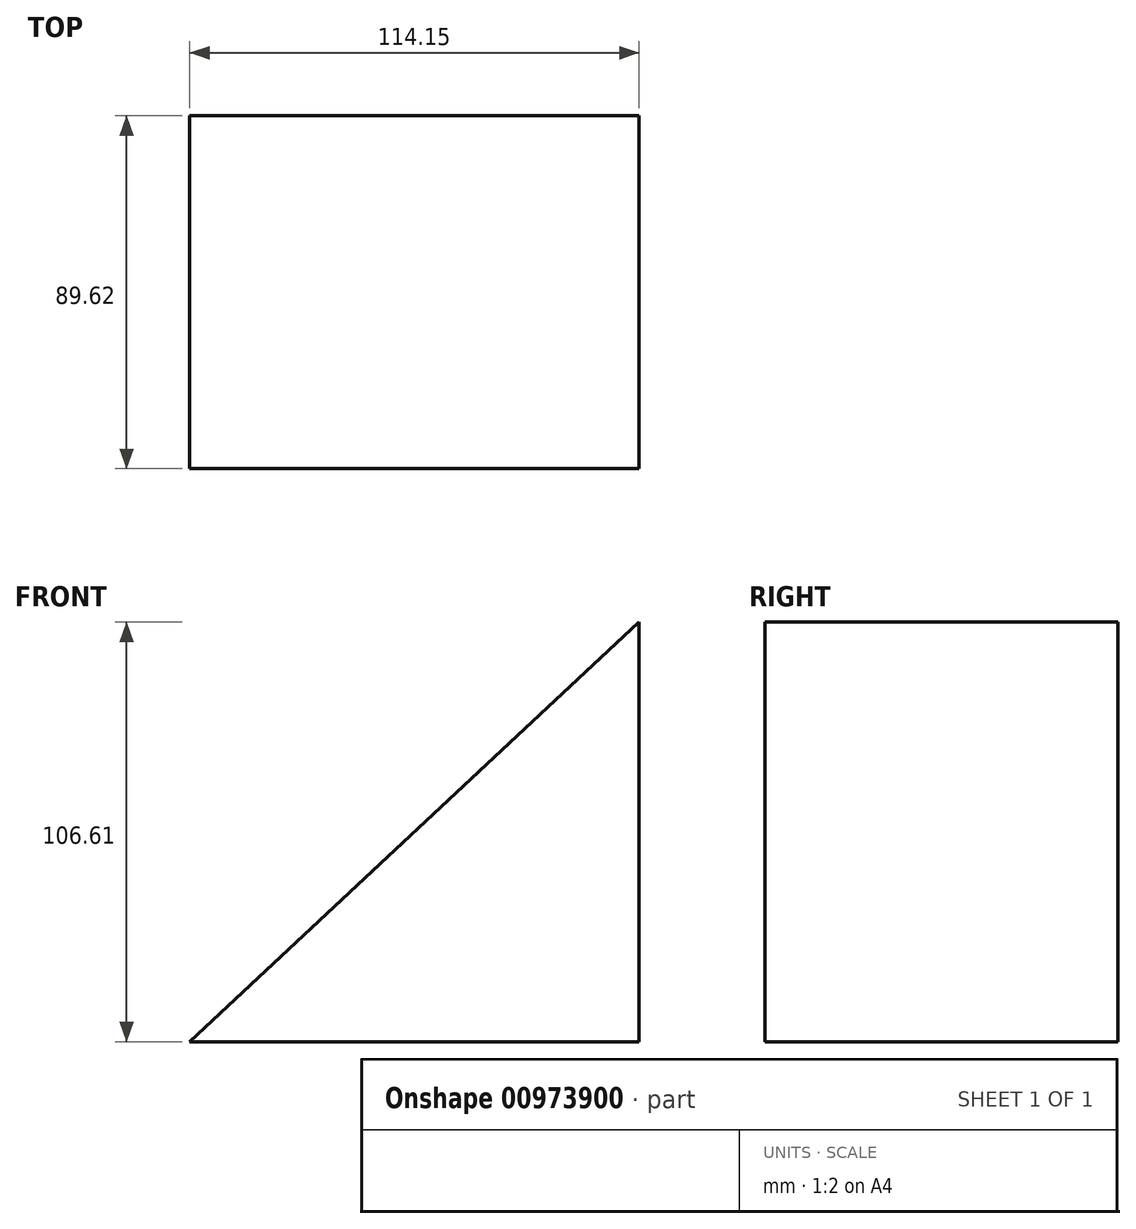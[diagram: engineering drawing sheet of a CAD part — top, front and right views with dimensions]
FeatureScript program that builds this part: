
annotation { "Feature Type Name" : "Feature", "Feature Type Description" : "" }
export const myFeature = defineFeature(function(context is Context, id is Id, definition is map)
    precondition{}
    {
        {
            var Q0;
            Q0=qCreatedBy(makeId("Front.planeOp"),FACE);
            var sketch = newSketch(context, id + "F0", { "sketchPlane" : qUnion([Q0])});
            skLineSegment(sketch, "E0", {"start": v(-49.12, -39.23) * mm, "end": v(65.03, -39.23) * mm});
            skLineSegment(sketch, "E1", {"start": v(65.03, -39.23) * mm, "end": v(65.03, 67.38) * mm});
            skLineSegment(sketch, "E2", {"start": v(65.03, 67.38) * mm, "end": v(-49.12, -39.23) * mm});
            skSolve(sketch);
        }
        {
            var Q0;
            Q0=makeQuery(id+"F0.imprint","IMPRINT",FACE,{"disambiguationData":[TD([[makeQuery(id+"F0.imprint","IMPRINT",EDGE,{"derivedFrom":sQuery(id+"F0.wireOp",EDGE,"E0")}),1.0]])]});
            extrude(context, id + "F1", {"entities" : qUnion([Q0]), "depth" : 89.62 * mm, "offsetDistance" : 25.4 * mm});
        }
    });
